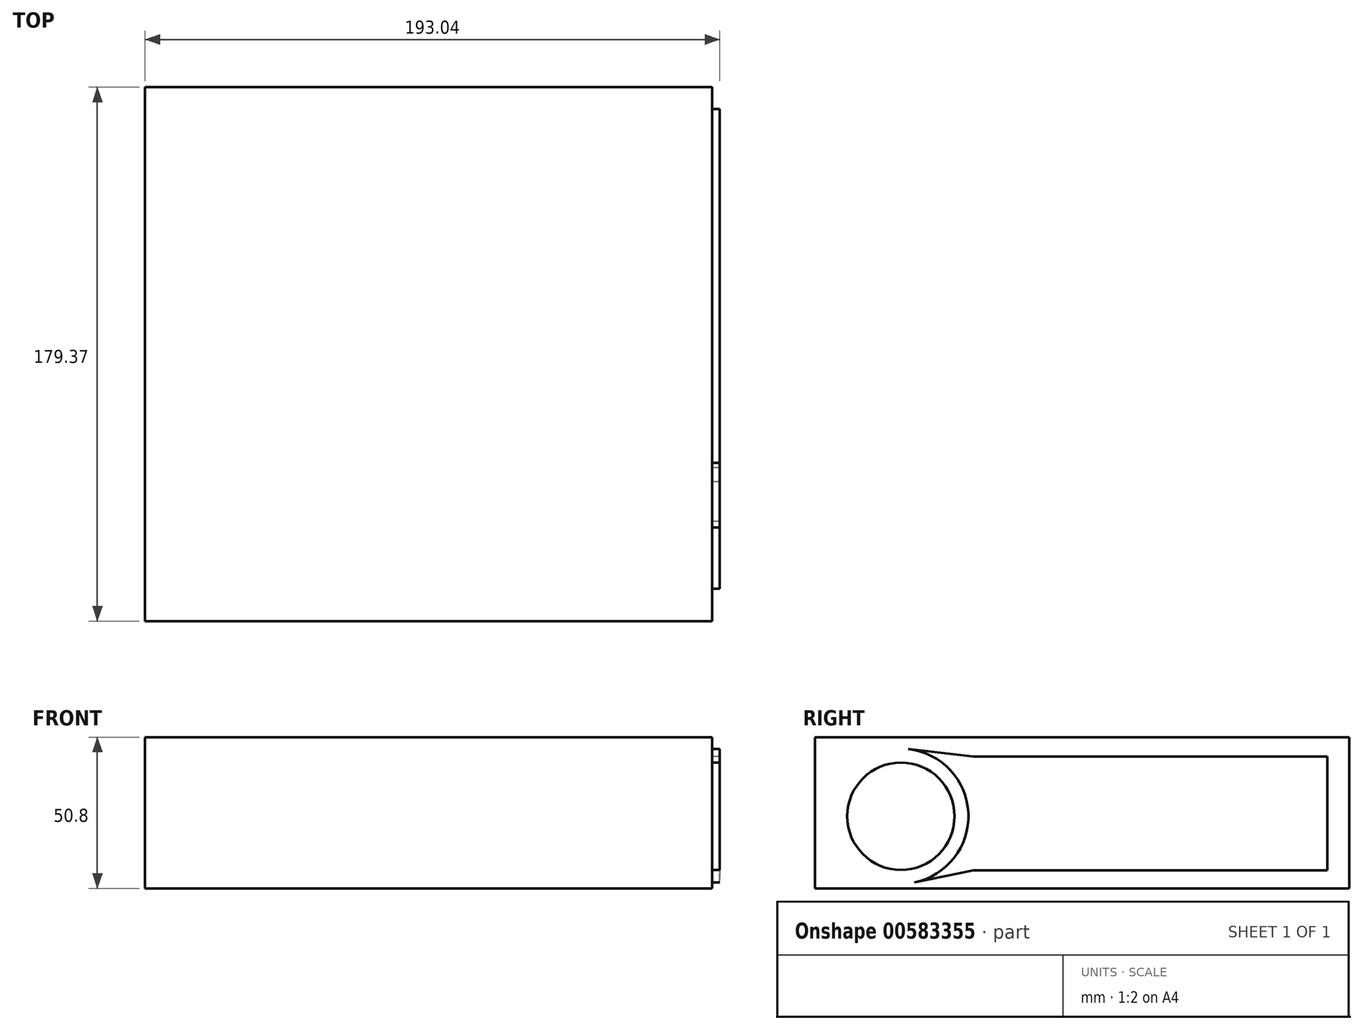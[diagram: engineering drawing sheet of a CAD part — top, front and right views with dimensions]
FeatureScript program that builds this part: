
annotation { "Feature Type Name" : "Feature", "Feature Type Description" : "" }
export const myFeature = defineFeature(function(context is Context, id is Id, definition is map)
    precondition{}
    {
        {
            var Q0;
            Q0=qCreatedBy(makeId("Front.planeOp"),FACE);
            var sketch = newSketch(context, id + "F0", { "sketchPlane" : qUnion([Q0])});
            skLineSegment(sketch, "E0.bottom", {"start": v(0, 0) * mm, "end": v(190.5, 0) * mm});
            skLineSegment(sketch, "E0.top", {"start": v(0, 50.8) * mm, "end": v(190.5, 50.8) * mm});
            skLineSegment(sketch, "E0.left", {"start": v(0, 0) * mm, "end": v(0, 50.8) * mm});
            skLineSegment(sketch, "E0.right", {"start": v(190.5, 0) * mm, "end": v(190.5, 50.8) * mm});
            skSolve(sketch);
        }
        {
            var Q0;
            Q0=qSketchRegion(id+"F0",true);
            extrude(context, id + "F1", {"entities" : qUnion([Q0]), "oppositeDirection" : true, "depth" : 179.37 * mm, "offsetDistance" : 25.4 * mm});
        }
        {
            var Q0;
            Q0=makeQuery(id+"F1.opExtrude","SWEPT_FACE",FACE,{"disambiguationData":[OSD([sQuery(id+"F0.wireOp",EDGE,"E0.right")])]});
            var sketch = newSketch(context, id + "F2", { "sketchPlane" : qUnion([Q0])});
            skCircle(sketch, "E1", {"center": v(28.83, 24.22) * mm, "radius": 18.03 * mm});
            skLineSegment(sketch, "E2.bottom", {"start": v(51.85, 42.21) * mm, "end": v(172.8, 42.21) * mm});
            skLineSegment(sketch, "E2.top", {"start": v(51.85, 8.34) * mm, "end": v(172.8, 8.34) * mm});
            skLineSegment(sketch, "E2.left", {"start": v(51.85, 42.21) * mm, "end": v(51.85, 8.34) * mm});
            skLineSegment(sketch, "E2.right", {"start": v(172.8, 42.21) * mm, "end": v(172.8, 8.34) * mm});
            skSolve(sketch);
        }
        {
            var Q0;
            Q0=makeQuery(id+"F2.imprint","IMPRINT",FACE,{"disambiguationData":[TD([[makeQuery(id+"F2.imprint","IMPRINT",EDGE,{"derivedFrom":sQuery(id+"F2.wireOp",EDGE,"E1")}),1.0]])]});
            extrude(context, id + "F3", {"entities" : qUnion([Q0]), "operationType" : NewBodyOperationType.ADD, "depth" : 2.54 * mm, "offsetDistance" : 25.4 * mm});
        }
        {
            var Q0;
            Q0=makeQuery(id+"F1.opExtrude","SWEPT_FACE",FACE,{"disambiguationData":[OSD([sQuery(id+"F0.wireOp",EDGE,"E0.right")])]});
            var sketch = newSketch(context, id + "F4", { "sketchPlane" : qUnion([Q0])});
            skArc(sketch, "E3", {"start": v(33.42, 2) * mm, "mid": v(51.5, 25.24) * mm, "end": v(31.4, 46.76) * mm});
            skLineSegment(sketch, "E4.bottom", {"start": v(53.2, 44.28) * mm, "end": v(172.03, 44.28) * mm});
            skLineSegment(sketch, "E4.top", {"start": v(53.2, 6.08) * mm, "end": v(172.03, 6.08) * mm});
            skLineSegment(sketch, "E4.right", {"start": v(172.03, 44.28) * mm, "end": v(172.03, 6.08) * mm});
            skLineSegment(sketch, "E5", {"start": v(53.2, 44.28) * mm, "end": v(31.4, 46.76) * mm});
            skLineSegment(sketch, "E6", {"start": v(53.2, 6.08) * mm, "end": v(33.42, 2) * mm});
            skSolve(sketch);
        }
        {
            var Q0;
            Q0=makeQuery(id+"F4.imprint","IMPRINT",FACE,{"disambiguationData":[TD([[makeQuery(id+"F4.imprint","IMPRINT",EDGE,{"derivedFrom":sQuery(id+"F4.wireOp",EDGE,"E3")}),-1.0]])]});
            extrude(context, id + "F5", {"entities" : qUnion([Q0]), "operationType" : NewBodyOperationType.ADD, "depth" : 2.54 * mm, "offsetDistance" : 25.4 * mm});
        }
    });
